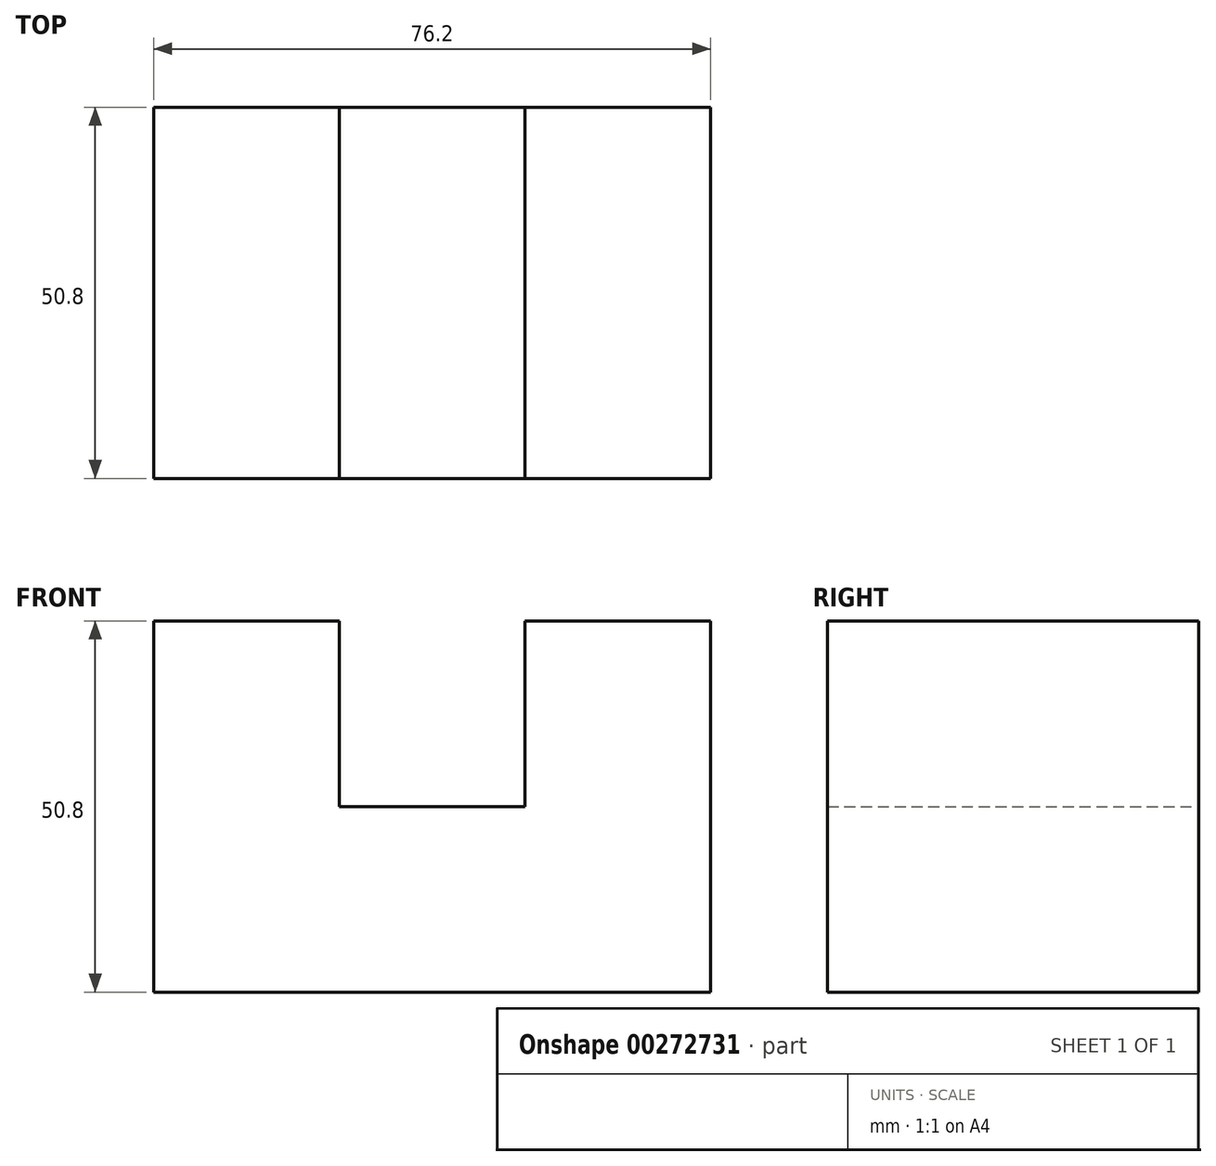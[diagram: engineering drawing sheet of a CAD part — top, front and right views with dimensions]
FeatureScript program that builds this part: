
annotation { "Feature Type Name" : "Feature", "Feature Type Description" : "" }
export const myFeature = defineFeature(function(context is Context, id is Id, definition is map)
    precondition{}
    {
        {
            var Q0;
            Q0=qCreatedBy(makeId("Front.planeOp"),FACE);
            var sketch = newSketch(context, id + "F0", { "sketchPlane" : qUnion([Q0])});
            skLineSegment(sketch, "E0", {"start": v(0, 0) * mm, "end": v(-76.2, 0) * mm});
            skLineSegment(sketch, "E1", {"start": v(-76.2, 0) * mm, "end": v(-76.2, 50.8) * mm});
            skLineSegment(sketch, "E2", {"start": v(-76.2, 50.8) * mm, "end": v(-50.8, 50.8) * mm});
            skLineSegment(sketch, "E3", {"start": v(-50.8, 50.8) * mm, "end": v(-50.8, 25.4) * mm});
            skLineSegment(sketch, "E4", {"start": v(-50.8, 25.4) * mm, "end": v(-25.4, 25.4) * mm});
            skLineSegment(sketch, "E5", {"start": v(-25.4, 25.4) * mm, "end": v(-25.4, 50.8) * mm});
            skLineSegment(sketch, "E6", {"start": v(-25.4, 50.8) * mm, "end": v(0, 50.8) * mm});
            skLineSegment(sketch, "E7", {"start": v(0, 50.8) * mm, "end": v(0, 0) * mm});
            skSolve(sketch);
        }
        {
            var Q0;
            Q0 = qSketchRegion(id + "F0", true);
            extrude(context, id + "F1", {"entities" : qUnion([Q0]), "depth" : 50.8 * mm});
        }
    });
